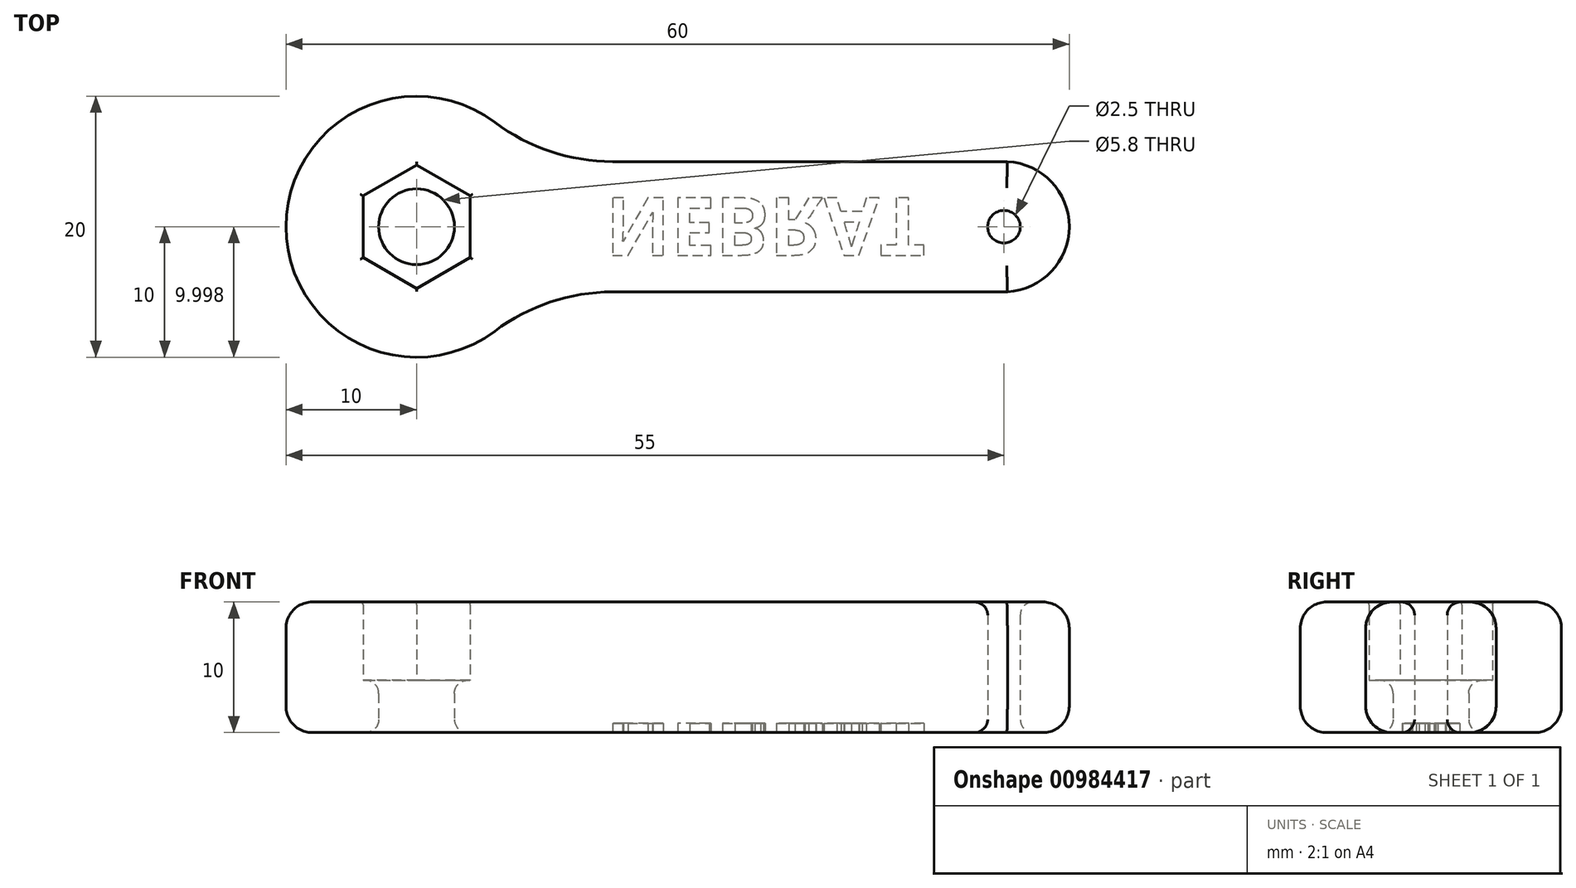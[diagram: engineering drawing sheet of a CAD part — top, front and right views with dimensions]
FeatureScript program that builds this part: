
annotation { "Feature Type Name" : "Feature", "Feature Type Description" : "" }
export const myFeature = defineFeature(function(context is Context, id is Id, definition is map)
    precondition{}
    {
        {
            var Q0;
            Q0=qCreatedBy(makeId("Top.planeOp"),FACE);
            var sketch = newSketch(context, id + "F0", { "sketchPlane" : qUnion([Q0])});
            skCircle(sketch, "E0.cCircle", {"center": v(0, 0) * mm, "radius": 4.1 * mm, "construction": true});
            skLineSegment(sketch, "E0.0", {"start": v(4.1, -2.36) * mm, "end": v(0, -4.73) * mm});
            skLineSegment(sketch, "E0.1", {"start": v(0, -4.73) * mm, "end": v(-4.1, -2.37) * mm});
            skLineSegment(sketch, "E0.2", {"start": v(-4.1, -2.37) * mm, "end": v(-4.1, 2.36) * mm});
            skLineSegment(sketch, "E0.3", {"start": v(-4.1, 2.36) * mm, "end": v(0, 4.73) * mm});
            skLineSegment(sketch, "E0.4", {"start": v(0, 4.73) * mm, "end": v(4.1, 2.37) * mm});
            skLineSegment(sketch, "E0.5", {"start": v(4.1, 2.37) * mm, "end": v(4.1, -2.36) * mm});
            skPoint(sketch, "E0.0.midPoint", {"position": v(2.05, -3.55) * mm});
            skArc(sketch, "E1", {"start": v(6, 8) * mm, "mid": v(0, 10) * mm, "end": v(-6, 8) * mm});
            skArc(sketch, "E2", {"start": v(44.73, -5) * mm, "mid": v(50, 0) * mm, "end": v(44.73, 5) * mm});
            skPoint(sketch, "E2.centerSnap0", {"position": v(-4.1, 0) * mm});
            skLineSegment(sketch, "E3", {"start": v(45.27, 5) * mm, "end": v(15.01, 5) * mm});
            skLineSegment(sketch, "E4", {"start": v(45.27, -5) * mm, "end": v(15, -5) * mm});
            skPoint(sketch, "E5.visualSharp", {"position": v(8.67, 5) * mm});
            skArc(sketch, "E5.filletArc", {"start": v(6, 8) * mm, "mid": v(10.26, 5.76) * mm, "end": v(15.01, 5) * mm});
            skPoint(sketch, "E6.visualSharp", {"position": v(8.66, -5) * mm});
            skArc(sketch, "E6.filletArc", {"start": v(15, -5) * mm, "mid": v(10.26, -5.77) * mm, "end": v(6, -8) * mm});
            skArc(sketch, "E7.trimOffspring", {"start": v(-6, -8) * mm, "mid": v(0, -10) * mm, "end": v(6, -8) * mm});
            skArc(sketch, "E8", {"start": v(-6, 8) * mm, "mid": v(-10, 0) * mm, "end": v(-6, -8) * mm});
            skCircle(sketch, "E9", {"center": v(45, 0) * mm, "radius": 1.25 * mm});
            skSolve(sketch);
        }
        {
            var Q0;
            Q0=makeQuery(id+"F0.imprint","IMPRINT",FACE,{"disambiguationData":[TD([[makeQuery(id+"F0.imprint","IMPRINT",EDGE,{"derivedFrom":sQuery(id+"F0.wireOp",EDGE,"E0.0")}),1.0]])]});
            extrude(context, id + "F1", {"entities" : qUnion([Q0]), "depth" : 10 * mm, "offsetDistance" : 25 * mm, "symmetric" : true});
        }
        {
            var Q0;
            Q0=makeQuery(id+"F1.opExtrude","CAP_FACE",FACE,{"disambiguationData":[OSD([sQuery(id+"F0.wireOp",EDGE,"E0.0"),sQuery(id+"F0.wireOp",EDGE,"E0.1"),sQuery(id+"F0.wireOp",EDGE,"E0.2"),sQuery(id+"F0.wireOp",EDGE,"E0.3"),sQuery(id+"F0.wireOp",EDGE,"E0.4"),sQuery(id+"F0.wireOp",EDGE,"E0.5"),sQuery(id+"F0.wireOp",EDGE,"E1"),sQuery(id+"F0.wireOp",EDGE,"E2"),sQuery(id+"F0.wireOp",EDGE,"E3"),sQuery(id+"F0.wireOp",EDGE,"E4"),sQuery(id+"F0.wireOp",EDGE,"E5.filletArc"),sQuery(id+"F0.wireOp",EDGE,"E6.filletArc"),sQuery(id+"F0.wireOp",EDGE,"749e59dd-aafc-4984-a9e9-d1398ae105bd0.MirrorCS"),sQuery(id+"F0.wireOp",EDGE,"dade7ec7-c57b-46b3-9a7e-9e8cd9d8b8f20.MirrorCS"),sQuery(id+"F0.wireOp",EDGE,"37e9966b-4a29-4a81-bcc0-c828a22c49ff0.MirrorCS"),sQuery(id+"F0.wireOp",EDGE,"2dd98768-d68a-4810-acd1-687a5160e65f0.MirrorCS"),sQuery(id+"F0.wireOp",EDGE,"7953b10d-258b-46b3-8019-80379e044c970.MirrorCS"),sQuery(id+"F0.wireOp",EDGE,"E7.trimOffspring")])],"isStart":true});
            var sketch = newSketch(context, id + "F2", { "sketchPlane" : qUnion([Q0])});
            skCircle(sketch, "E10", {"center": v(0, 0) * mm, "radius": 6.45 * mm});
            skCircle(sketch, "E11", {"center": v(0, 0) * mm, "radius": 2.9 * mm});
            skSolve(sketch);
        }
        {
            var Q0;
            Q0=qSketchRegion(id+"F2",true);
            extrude(context, id + "F3", {"entities" : qUnion([Q0]), "operationType" : NewBodyOperationType.ADD, "oppositeDirection" : true, "depth" : 4 * mm, "offsetDistance" : 25 * mm});
        }
        {
            var Q0;
            Q0=makeQuery(id+"F1.opExtrude","CAP_EDGE",EDGE,{"disambiguationData":[OSD([sQuery(id+"F0.wireOp",EDGE,"E0.3")])],"isStart":false});
            var Q1;
            Q1=makeQuery(id+"F1.opExtrude","CAP_EDGE",EDGE,{"disambiguationData":[OSD([sQuery(id+"F0.wireOp",EDGE,"E0.4")])],"isStart":false});
            var Q2;
            Q2=makeQuery(id+"F1.opExtrude","CAP_EDGE",EDGE,{"disambiguationData":[OSD([sQuery(id+"F0.wireOp",EDGE,"E0.5")])],"isStart":false});
            var Q3;
            Q3=makeQuery(id+"F1.opExtrude","CAP_EDGE",EDGE,{"disambiguationData":[OSD([sQuery(id+"F0.wireOp",EDGE,"E0.0")])],"isStart":false});
            var Q4;
            Q4=makeQuery(id+"F1.opExtrude","CAP_EDGE",EDGE,{"disambiguationData":[OSD([sQuery(id+"F0.wireOp",EDGE,"E0.1")])],"isStart":false});
            var Q5;
            Q5=makeQuery(id+"F1.opExtrude","CAP_EDGE",EDGE,{"disambiguationData":[OSD([sQuery(id+"F0.wireOp",EDGE,"E0.2")])],"isStart":false});
            fillet(context, id + "F4", {"entities" : qUnion([Q0, Q1, Q2, Q3, Q4, Q5]), "radius" : 0.2 * mm, "tangentPropagation" : true, "allowEdgeOverflow" : false});
        }
        {
            var Q0;
            Q0=makeQuery(id+"F3.boolean.opBoolean","MERGE",FACE,{"derivedFrom":[makeQuery(id+"F1.opExtrude","CAP_FACE",FACE,{"disambiguationData":[OSD([sQuery(id+"F0.wireOp",EDGE,"E0.0"),sQuery(id+"F0.wireOp",EDGE,"E0.1"),sQuery(id+"F0.wireOp",EDGE,"E0.2"),sQuery(id+"F0.wireOp",EDGE,"E0.3"),sQuery(id+"F0.wireOp",EDGE,"E0.4"),sQuery(id+"F0.wireOp",EDGE,"E0.5"),sQuery(id+"F0.wireOp",EDGE,"E1"),sQuery(id+"F0.wireOp",EDGE,"E2"),sQuery(id+"F0.wireOp",EDGE,"E3"),sQuery(id+"F0.wireOp",EDGE,"E4"),sQuery(id+"F0.wireOp",EDGE,"E5.filletArc"),sQuery(id+"F0.wireOp",EDGE,"E6.filletArc"),sQuery(id+"F0.wireOp",EDGE,"749e59dd-aafc-4984-a9e9-d1398ae105bd0.MirrorCS"),sQuery(id+"F0.wireOp",EDGE,"dade7ec7-c57b-46b3-9a7e-9e8cd9d8b8f20.MirrorCS"),sQuery(id+"F0.wireOp",EDGE,"37e9966b-4a29-4a81-bcc0-c828a22c49ff0.MirrorCS"),sQuery(id+"F0.wireOp",EDGE,"2dd98768-d68a-4810-acd1-687a5160e65f0.MirrorCS"),sQuery(id+"F0.wireOp",EDGE,"7953b10d-258b-46b3-8019-80379e044c970.MirrorCS"),sQuery(id+"F0.wireOp",EDGE,"E7.trimOffspring")])],"isStart":true}),makeQuery(id+"F3.opExtrude","CAP_FACE",FACE,{"disambiguationData":[OSD([sQuery(id+"F2.wireOp",EDGE,"E10")])],"isStart":true})]});
            var sketch = newSketch(context, id + "F5", { "sketchPlane" : qUnion([Q0])});
            skText(sketch, "E12", { "text": "NEBRAT", "fontName": "OpenSans-Bold.ttf"});
            const initialGuessF5  = {"E12": [0.01447, -0.0022, 1, 0, 0.00442]};
            skSetInitialGuess(sketch, initialGuessF5);
            skSolve(sketch);
        }
        {
            var Q0;
            Q0 = qSketchRegion(id + "F5", true);
            extrude(context, id + "F6", {"entities" : qUnion([Q0]), "operationType" : NewBodyOperationType.REMOVE, "oppositeDirection" : true, "depth" : 0.7 * mm, "offsetDistance" : 25 * mm});
        }
        {
            var Q0;
            Q0=makeQuery(id+"F1.opExtrude","CAP_EDGE",EDGE,{"disambiguationData":[OSD([sQuery(id+"F0.wireOp",EDGE,"E2")])],"isStart":true});
            var Q1;
            Q1=makeQuery(id+"F1.opExtrude","CAP_EDGE",EDGE,{"disambiguationData":[OSD([sQuery(id+"F0.wireOp",EDGE,"E3")])],"isStart":true});
            var Q2;
            Q2=makeQuery(id+"F1.opExtrude","CAP_EDGE",EDGE,{"disambiguationData":[OSD([sQuery(id+"F0.wireOp",EDGE,"E5.filletArc")])],"isStart":true});
            var Q3;
            Q3=makeQuery(id+"F1.opExtrude","CAP_EDGE",EDGE,{"disambiguationData":[OSD([sQuery(id+"F0.wireOp",EDGE,"E1")])],"isStart":true});
            var Q4;
            Q4=makeQuery(id+"F1.opExtrude","CAP_EDGE",EDGE,{"disambiguationData":[OSD([sQuery(id+"F0.wireOp",EDGE,"749e59dd-aafc-4984-a9e9-d1398ae105bd0.MirrorCS")])],"isStart":true});
            var Q5;
            Q5=makeQuery(id+"F1.opExtrude","CAP_EDGE",EDGE,{"disambiguationData":[OSD([sQuery(id+"F0.wireOp",EDGE,"dade7ec7-c57b-46b3-9a7e-9e8cd9d8b8f20.MirrorCS")])],"isStart":true});
            var Q6;
            Q6=makeQuery(id+"F1.opExtrude","CAP_EDGE",EDGE,{"disambiguationData":[OSD([sQuery(id+"F0.wireOp",EDGE,"37e9966b-4a29-4a81-bcc0-c828a22c49ff0.MirrorCS")])],"isStart":true});
            var Q7;
            Q7=makeQuery(id+"F1.opExtrude","CAP_EDGE",EDGE,{"disambiguationData":[OSD([sQuery(id+"F0.wireOp",EDGE,"2dd98768-d68a-4810-acd1-687a5160e65f0.MirrorCS")])],"isStart":true});
            var Q8;
            Q8=makeQuery(id+"F1.opExtrude","CAP_EDGE",EDGE,{"disambiguationData":[OSD([sQuery(id+"F0.wireOp",EDGE,"7953b10d-258b-46b3-8019-80379e044c970.MirrorCS")])],"isStart":true});
            var Q9;
            Q9=makeQuery(id+"F1.opExtrude","CAP_EDGE",EDGE,{"disambiguationData":[OSD([sQuery(id+"F0.wireOp",EDGE,"E7.trimOffspring")])],"isStart":true});
            var Q10;
            Q10=makeQuery(id+"F1.opExtrude","CAP_EDGE",EDGE,{"disambiguationData":[OSD([sQuery(id+"F0.wireOp",EDGE,"E6.filletArc")])],"isStart":true});
            var Q11;
            Q11=makeQuery(id+"F1.opExtrude","CAP_EDGE",EDGE,{"disambiguationData":[OSD([sQuery(id+"F0.wireOp",EDGE,"E4")])],"isStart":true});
            var Q12;
            Q12=makeQuery(id+"F1.opExtrude","CAP_EDGE",EDGE,{"disambiguationData":[OSD([sQuery(id+"F0.wireOp",EDGE,"dade7ec7-c57b-46b3-9a7e-9e8cd9d8b8f20.MirrorCS")])],"isStart":false});
            var Q13;
            Q13=makeQuery(id+"F1.opExtrude","CAP_EDGE",EDGE,{"disambiguationData":[OSD([sQuery(id+"F0.wireOp",EDGE,"749e59dd-aafc-4984-a9e9-d1398ae105bd0.MirrorCS")])],"isStart":false});
            var Q14;
            Q14=makeQuery(id+"F1.opExtrude","CAP_EDGE",EDGE,{"disambiguationData":[OSD([sQuery(id+"F0.wireOp",EDGE,"E1")])],"isStart":false});
            var Q15;
            Q15=makeQuery(id+"F1.opExtrude","CAP_EDGE",EDGE,{"disambiguationData":[OSD([sQuery(id+"F0.wireOp",EDGE,"E5.filletArc")])],"isStart":false});
            var Q16;
            Q16=makeQuery(id+"F1.opExtrude","CAP_EDGE",EDGE,{"disambiguationData":[OSD([sQuery(id+"F0.wireOp",EDGE,"E3")])],"isStart":false});
            var Q17;
            Q17=makeQuery(id+"F1.opExtrude","CAP_EDGE",EDGE,{"disambiguationData":[OSD([sQuery(id+"F0.wireOp",EDGE,"E2")])],"isStart":false});
            var Q18;
            Q18=makeQuery(id+"F1.opExtrude","CAP_EDGE",EDGE,{"disambiguationData":[OSD([sQuery(id+"F0.wireOp",EDGE,"E4")])],"isStart":false});
            var Q19;
            Q19=makeQuery(id+"F1.opExtrude","CAP_EDGE",EDGE,{"disambiguationData":[OSD([sQuery(id+"F0.wireOp",EDGE,"E6.filletArc")])],"isStart":false});
            var Q20;
            Q20=makeQuery(id+"F1.opExtrude","CAP_EDGE",EDGE,{"disambiguationData":[OSD([sQuery(id+"F0.wireOp",EDGE,"E7.trimOffspring")])],"isStart":false});
            var Q21;
            Q21=makeQuery(id+"F1.opExtrude","CAP_EDGE",EDGE,{"disambiguationData":[OSD([sQuery(id+"F0.wireOp",EDGE,"7953b10d-258b-46b3-8019-80379e044c970.MirrorCS")])],"isStart":false});
            var Q22;
            Q22=makeQuery(id+"F1.opExtrude","CAP_EDGE",EDGE,{"disambiguationData":[OSD([sQuery(id+"F0.wireOp",EDGE,"2dd98768-d68a-4810-acd1-687a5160e65f0.MirrorCS")])],"isStart":false});
            var Q23;
            Q23=makeQuery(id+"F1.opExtrude","CAP_EDGE",EDGE,{"disambiguationData":[OSD([sQuery(id+"F0.wireOp",EDGE,"37e9966b-4a29-4a81-bcc0-c828a22c49ff0.MirrorCS")])],"isStart":false});
            fillet(context, id + "F7", {"entities" : qUnion([Q0, Q1, Q2, Q3, Q4, Q5, Q6, Q7, Q8, Q9, Q10, Q11, Q12, Q13, Q14, Q15, Q16, Q17, Q18, Q19, Q20, Q21, Q22, Q23]), "radius" : 2 * mm, "tangentPropagation" : true, "allowEdgeOverflow" : false});
        }
        {
            var Q0;
            Q0=makeQuery(id+"F3.opExtrude","CAP_EDGE",EDGE,{"disambiguationData":[OSD([sQuery(id+"F2.wireOp",EDGE,"E11")])],"isStart":false});
            var Q1;
            Q1=makeQuery(id+"F3.opExtrude","CAP_EDGE",EDGE,{"disambiguationData":[OSD([sQuery(id+"F2.wireOp",EDGE,"E11")])],"isStart":true});
            var Q2;
            Q2=makeQuery(id+"F1.opExtrude","CAP_EDGE",EDGE,{"disambiguationData":[OSD([sQuery(id+"F0.wireOp",EDGE,"E9")])],"isStart":false});
            var Q3;
            Q3=makeQuery(id+"F1.opExtrude","CAP_EDGE",EDGE,{"disambiguationData":[OSD([sQuery(id+"F0.wireOp",EDGE,"E9")])],"isStart":true});
            fillet(context, id + "F8", {"entities" : qUnion([Q0, Q1, Q2, Q3]), "radius" : 1 * mm, "tangentPropagation" : true, "allowEdgeOverflow" : false});
        }
    });
